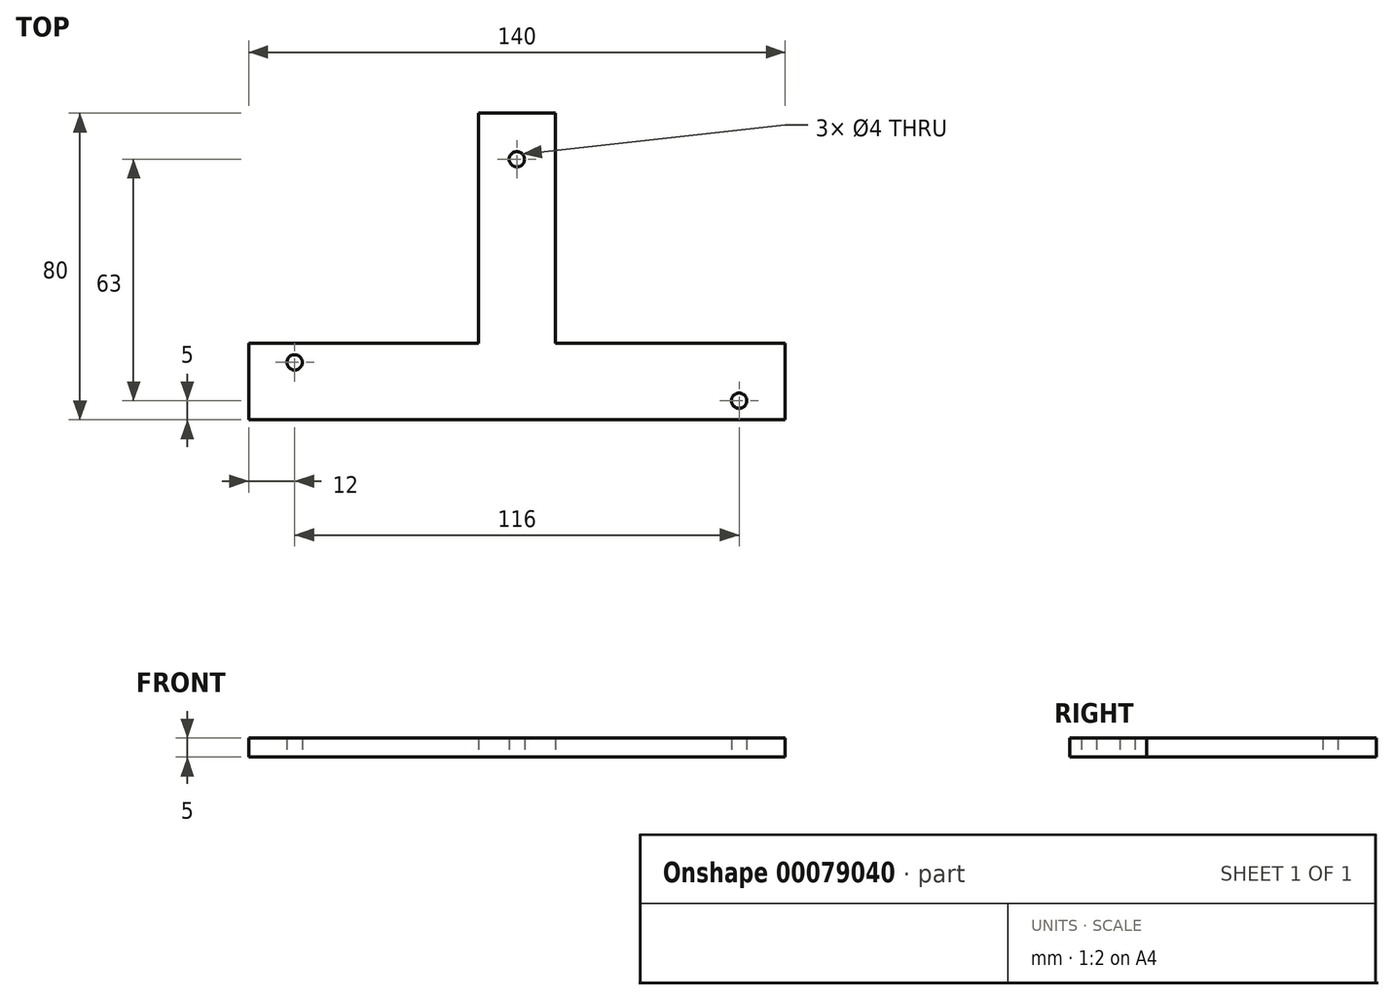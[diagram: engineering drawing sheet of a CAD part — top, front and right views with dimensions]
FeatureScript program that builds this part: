
annotation { "Feature Type Name" : "Feature", "Feature Type Description" : "" }
export const myFeature = defineFeature(function(context is Context, id is Id, definition is map)
    precondition{}
    {
        {
            var Q0;
            Q0=qCreatedBy(makeId("Top.planeOp"),FACE);
            var sketch = newSketch(context, id + "F0", { "sketchPlane" : qUnion([Q0])});
            skLineSegment(sketch, "E0.bottom", {"start": v(70, 10) * mm, "end": v(10, 10) * mm});
            skLineSegment(sketch, "E0.top", {"start": v(70, -10) * mm, "end": v(-70, -10) * mm});
            skLineSegment(sketch, "E0.left", {"start": v(70, 10) * mm, "end": v(70, -10) * mm});
            skLineSegment(sketch, "E0.right", {"start": v(-70, 10) * mm, "end": v(-70, -10) * mm});
            skPoint(sketch, "E0.middle", {"position": v(0, 0) * mm});
            skLineSegment(sketch, "E1.top", {"start": v(-10, 70) * mm, "end": v(10, 70) * mm});
            skLineSegment(sketch, "E1.left", {"start": v(10, 10) * mm, "end": v(10, 70) * mm});
            skLineSegment(sketch, "E1.right", {"start": v(-10, 10) * mm, "end": v(-10, 70) * mm});
            skLineSegment(sketch, "E2.trimOffspring", {"start": v(-10, 10) * mm, "end": v(-70, 10) * mm});
            skCircle(sketch, "E3", {"center": v(-58, 5) * mm, "radius": 2 * mm});
            skCircle(sketch, "E4", {"center": v(0, 58) * mm, "radius": 2 * mm});
            skCircle(sketch, "E5", {"center": v(58, -5) * mm, "radius": 2 * mm});
            skSolve(sketch);
        }
        {
            var Q0;
            Q0=makeQuery(id+"F0.imprint","IMPRINT",FACE,{"disambiguationData":[TD([[makeQuery(id+"F0.imprint","IMPRINT",EDGE,{"derivedFrom":sQuery(id+"F0.wireOp",EDGE,"E0.bottom")}),1.0]])]});
            extrude(context, id + "F1", {"entities" : qUnion([Q0]), "depth" : 5 * mm});
        }
    });
